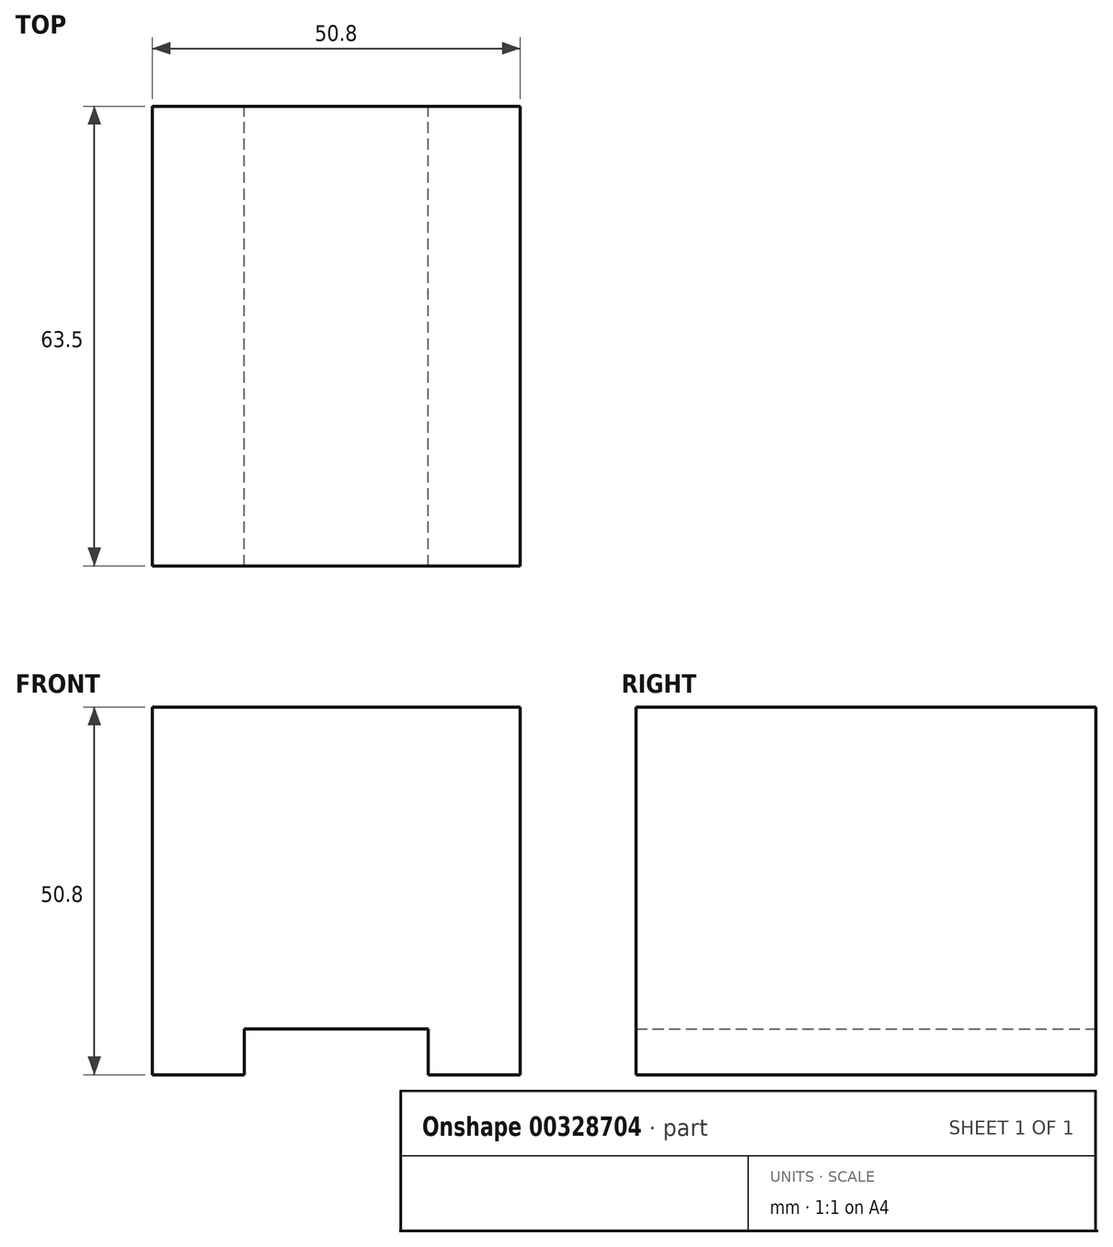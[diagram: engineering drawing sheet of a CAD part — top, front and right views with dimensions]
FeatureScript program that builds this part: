
annotation { "Feature Type Name" : "Feature", "Feature Type Description" : "" }
export const myFeature = defineFeature(function(context is Context, id is Id, definition is map)
    precondition{}
    {
        {
            var Q0;
            Q0=qCreatedBy(makeId("Front.planeOp"),FACE);
            var sketch = newSketch(context, id + "F0", { "sketchPlane" : qUnion([Q0])});
            skLineSegment(sketch, "E0.bottom", {"start": v(25.4, 25.4) * mm, "end": v(-25.4, 25.4) * mm});
            skLineSegment(sketch, "E0.top", {"start": v(25.4, -25.4) * mm, "end": v(12.7, -25.4) * mm});
            skLineSegment(sketch, "E0.left", {"start": v(25.4, 25.4) * mm, "end": v(25.4, -25.4) * mm});
            skLineSegment(sketch, "E0.right", {"start": v(-25.4, 25.4) * mm, "end": v(-25.4, -25.4) * mm});
            skPoint(sketch, "E0.middle", {"position": v(0, 0) * mm});
            skLineSegment(sketch, "E1.0", {"start": v(12.7, -19.05) * mm, "end": v(-12.7, -19.05) * mm});
            skLineSegment(sketch, "E2.0", {"start": v(12.7, -19.05) * mm, "end": v(12.7, -25.4) * mm});
            skLineSegment(sketch, "E3.0", {"start": v(-12.7, -19.05) * mm, "end": v(-12.7, -25.4) * mm});
            skLineSegment(sketch, "E4.trimOffspring", {"start": v(-12.7, -25.4) * mm, "end": v(-25.4, -25.4) * mm});
            skSolve(sketch);
        }
        {
            var Q0;
            Q0 = qSketchRegion(id + "F0", true);
            extrude(context, id + "F1", {"entities" : qUnion([Q0]), "depth" : 63.5 * mm});
        }
    });
